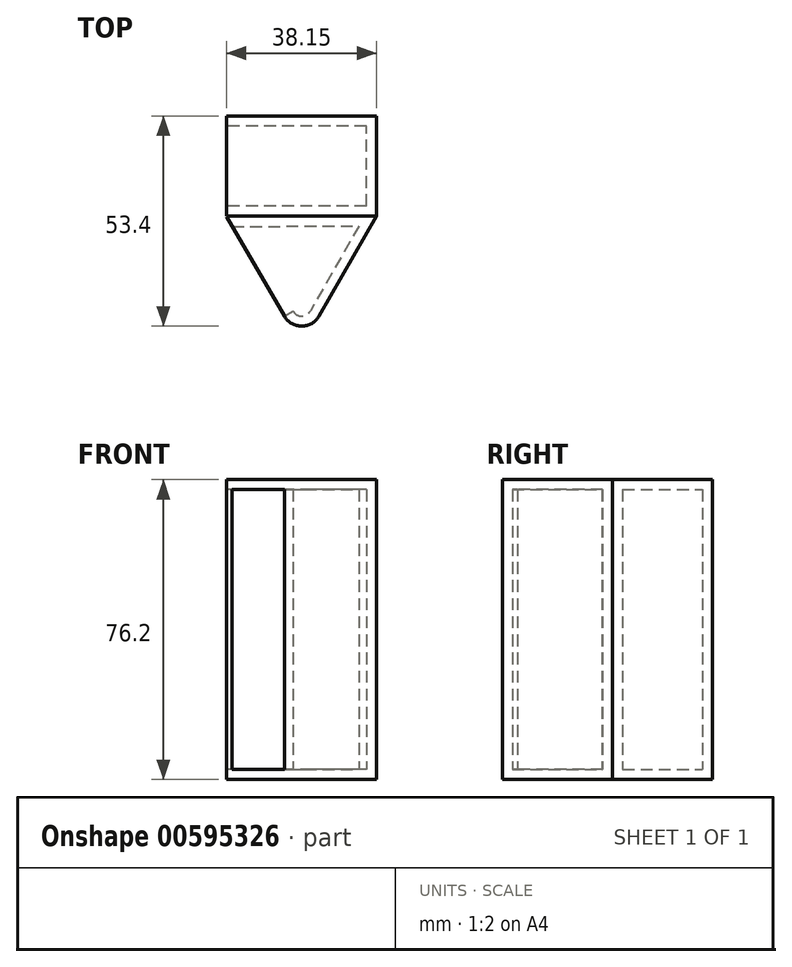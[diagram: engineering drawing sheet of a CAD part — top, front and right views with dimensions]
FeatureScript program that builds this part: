
annotation { "Feature Type Name" : "Feature", "Feature Type Description" : "" }
export const myFeature = defineFeature(function(context is Context, id is Id, definition is map)
    precondition{}
    {
        {
            var Q0;
            Q0=qCreatedBy(makeId("Top.planeOp"),FACE);
            var sketch = newSketch(context, id + "F0", { "sketchPlane" : qUnion([Q0])});
            skLineSegment(sketch, "E0.bottom", {"start": v(0, 0) * mm, "end": v(-38.1, 0) * mm});
            skLineSegment(sketch, "E0.top", {"start": v(0, 25.4) * mm, "end": v(-38.1, 25.4) * mm});
            skLineSegment(sketch, "E0.left", {"start": v(0, 0) * mm, "end": v(0, 25.4) * mm});
            skLineSegment(sketch, "E0.right", {"start": v(-38.1, 0) * mm, "end": v(-38.1, 25.4) * mm});
            skCircle(sketch, "E1.cCircle", {"center": v(-19.05, -11.08) * mm, "radius": 11 * mm, "construction": true});
            skLineSegment(sketch, "E1.0", {"start": v(-0.05, 0) * mm, "end": v(-18.96, -33.08) * mm});
            skLineSegment(sketch, "E1.1", {"start": v(-18.96, -33.08) * mm, "end": v(-38.15, -0.16) * mm});
            skLineSegment(sketch, "E1.2", {"start": v(-38.15, -0.16) * mm, "end": v(-0.05, 0) * mm});
            skPoint(sketch, "E1.0.midPoint", {"position": v(-9.5, -16.54) * mm});
            skSolve(sketch);
        }
        {
            var Q0;
            Q0=makeQuery(id+"F0.imprint","IMPRINT",FACE,{"disambiguationData":[TD([[makeQuery(id+"F0.imprint","IMPRINT",EDGE,{"derivedFrom":sQuery(id+"F0.wireOp",EDGE,"E1.0")}),-1.0]])]});
            var Q1;
            Q1=makeQuery(id+"F0.imprint","IMPRINT",FACE,{"disambiguationData":[TD([[makeQuery(id+"F0.imprint","IMPRINT",EDGE,{"derivedFrom":sQuery(id+"F0.wireOp",EDGE,"E0.top")}),1.0]])]});
            extrude(context, id + "F1", {"entities" : qUnion([Q0, Q1]), "depth" : 76.2 * mm, "offsetDistance" : 25.4 * mm});
        }
        {
            var Q0;
            Q0=makeQuery(id+"F1.opExtrude","SWEPT_EDGE",EDGE,{"disambiguationData":[OSD([sQuery(id+"F0.wireOp",EDGE,"E1.0"),sQuery(id+"F0.wireOp",EDGE,"E1.1")])]});
            fillet(context, id + "F2", {"entities" : qUnion([Q0]), "radius" : 5.08 * mm, "tangentPropagation" : true, "allowEdgeOverflow" : false});
        }
        {
            var Q0;
            Q0=makeQuery(id+"F1.opExtrude","SWEPT_FACE",FACE,{"disambiguationData":[OSD([sQuery(id+"F0.wireOp",EDGE,"E0.right")])]});
            var Q1;
            Q1=makeQuery(id+"F1.opExtrude","SWEPT_FACE",FACE,{"disambiguationData":[OSD([sQuery(id+"F0.wireOp",EDGE,"E1.1")])]});
            shell(context, id + "F3", {"entities" : qUnion([Q0, Q1]), "thickness" : 2.54 * mm});
        }
    });
